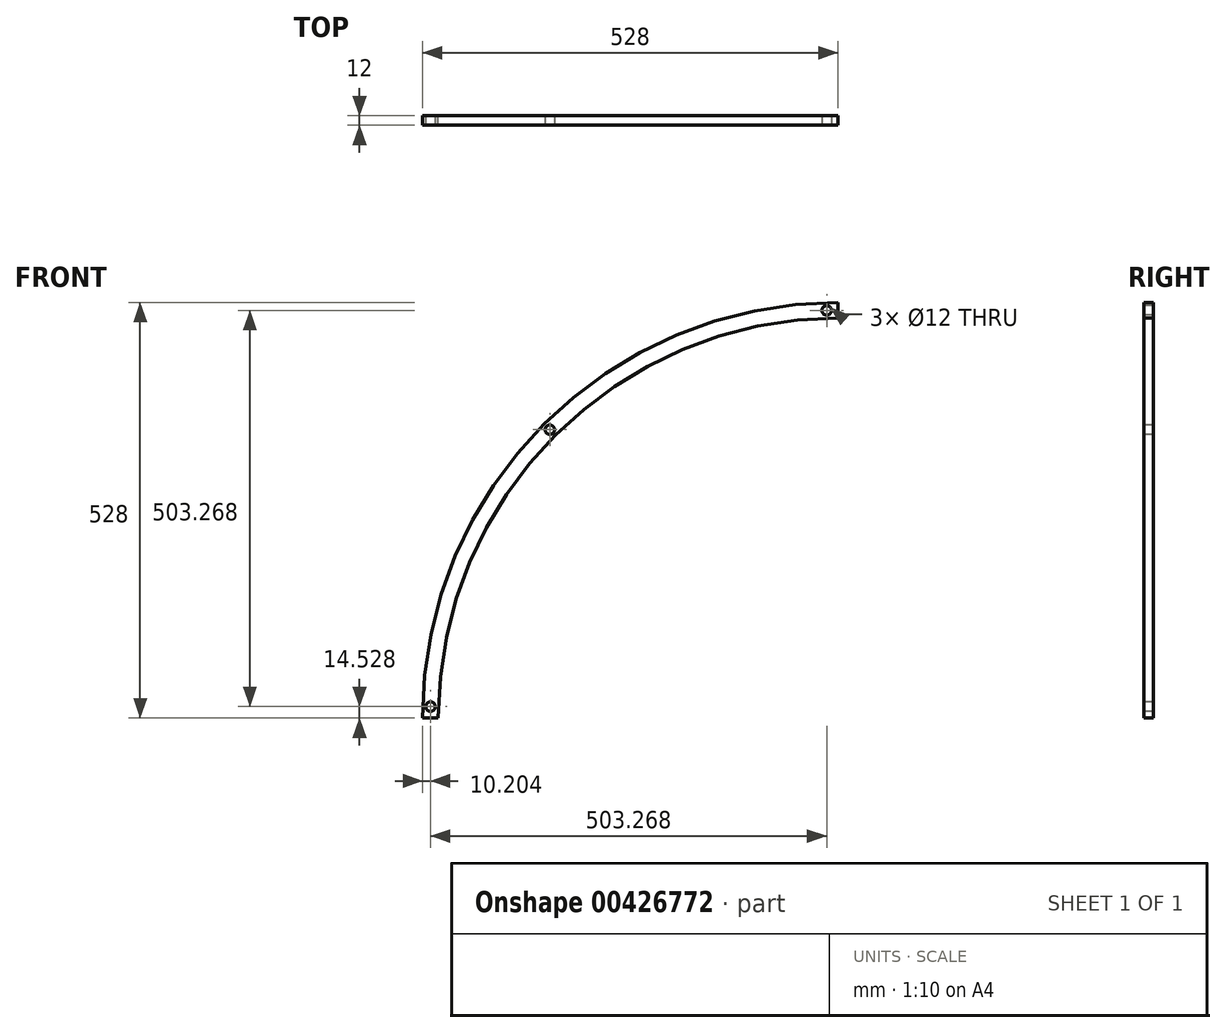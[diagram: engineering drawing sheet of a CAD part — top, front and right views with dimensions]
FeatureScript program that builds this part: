
annotation { "Feature Type Name" : "Feature", "Feature Type Description" : "" }
export const myFeature = defineFeature(function(context is Context, id is Id, definition is map)
    precondition{}
    {
        {
            var Q0;
            Q0=qCreatedBy(makeId("Front.planeOp"),FACE);
            var sketch = newSketch(context, id + "F0", { "sketchPlane" : qUnion([Q0])});
            skCircle(sketch, "E0", {"center": v(0, 0) * mm, "radius": 508 * mm});
            skCircle(sketch, "E1", {"center": v(0, 0) * mm, "radius": 528 * mm});
            skCircle(sketch, "E2", {"center": v(0, 0) * mm, "radius": 518 * mm, "construction": true});
            skLineSegment(sketch, "E3", {"start": v(0, 0) * mm, "end": v(0, 528) * mm});
            skLineSegment(sketch, "E4", {"start": v(0, 0) * mm, "end": v(-528, 0) * mm});
            skSolve(sketch);
        }
        {
            var Q0;
            {var subQ0=sQuery(id+"F0.wireOp",EDGE,"E3");var subQ1=sQuery(id+"F0.wireOp",EDGE,"E0");var subQ2=makeQuery(id+"F0.imprint","INTERSECT",VERTEX,{"derivedFrom":[subQ1,subQ0]});Q0=makeQuery(id+"F0.imprint","IMPRINT",FACE,{"disambiguationData":[TD([[makeQuery(id+"F0.imprint","IMPRINT",EDGE,{"disambiguationData":[TD([[subQ2,-1.0]])],"derivedFrom":subQ1}),-1.0]])]});}
            extrude(context, id + "F1", {"entities" : qUnion([Q0]), "depth" : 12 * mm});
        }
        {
            var Q0;
            Q0=makeQuery(id+"F1.opExtrude","CAP_FACE",FACE,{"disambiguationData":[OSD([sQuery(id+"F0.wireOp",EDGE,"E0"),sQuery(id+"F0.wireOp",EDGE,"E1")])],"isStart":false});
            var sketch = newSketch(context, id + "F2", { "sketchPlane" : qUnion([Q0])});
            skArc(sketch, "E5", {"start": v(-14.53, 517.8) * mm, "mid": v(-380.53, 351.46) * mm, "end": v(-517.32, -26.58) * mm, "construction": true});
            skCircle(sketch, "E6", {"center": v(-14.53, 517.8) * mm, "radius": 6 * mm});
            skCircle(sketch, "E7.1.0", {"center": v(-366.28, 366.28) * mm, "radius": 6 * mm});
            skCircle(sketch, "E7.2.0", {"center": v(-517.8, 14.53) * mm, "radius": 6 * mm});
            skLineSegment(sketch, "E7.anchor1", {"start": v(0, 0) * mm, "end": v(-14.53, 517.8) * mm, "construction": true});
            skLineSegment(sketch, "E7.anchor2", {"start": v(0, 0) * mm, "end": v(-517.8, 14.53) * mm, "construction": true});
            skSolve(sketch);
        }
        {
            var Q0;
            Q0=makeQuery(id+"F2.imprint","IMPRINT",FACE,{"disambiguationData":[TD([[makeQuery(id+"F2.imprint","IMPRINT",EDGE,{"derivedFrom":sQuery(id+"F2.wireOp",EDGE,"E6")}),1.0]])]});
            var Q1;
            Q1=makeQuery(id+"F2.imprint","IMPRINT",FACE,{"disambiguationData":[TD([[makeQuery(id+"F2.imprint","IMPRINT",EDGE,{"derivedFrom":sQuery(id+"F2.wireOp",EDGE,"E7.1.0")}),1.0]])]});
            var Q2;
            Q2=makeQuery(id+"F2.imprint","IMPRINT",FACE,{"disambiguationData":[TD([[makeQuery(id+"F2.imprint","IMPRINT",EDGE,{"derivedFrom":sQuery(id+"F2.wireOp",EDGE,"E7.2.0")}),1.0]])]});
            extrude(context, id + "F3", {"entities" : qUnion([Q0, Q1, Q2]), "operationType" : NewBodyOperationType.REMOVE, "endBound" : BoundingType.THROUGH_ALL, "oppositeDirection" : true, "depth" : 25 * mm});
        }
    });
